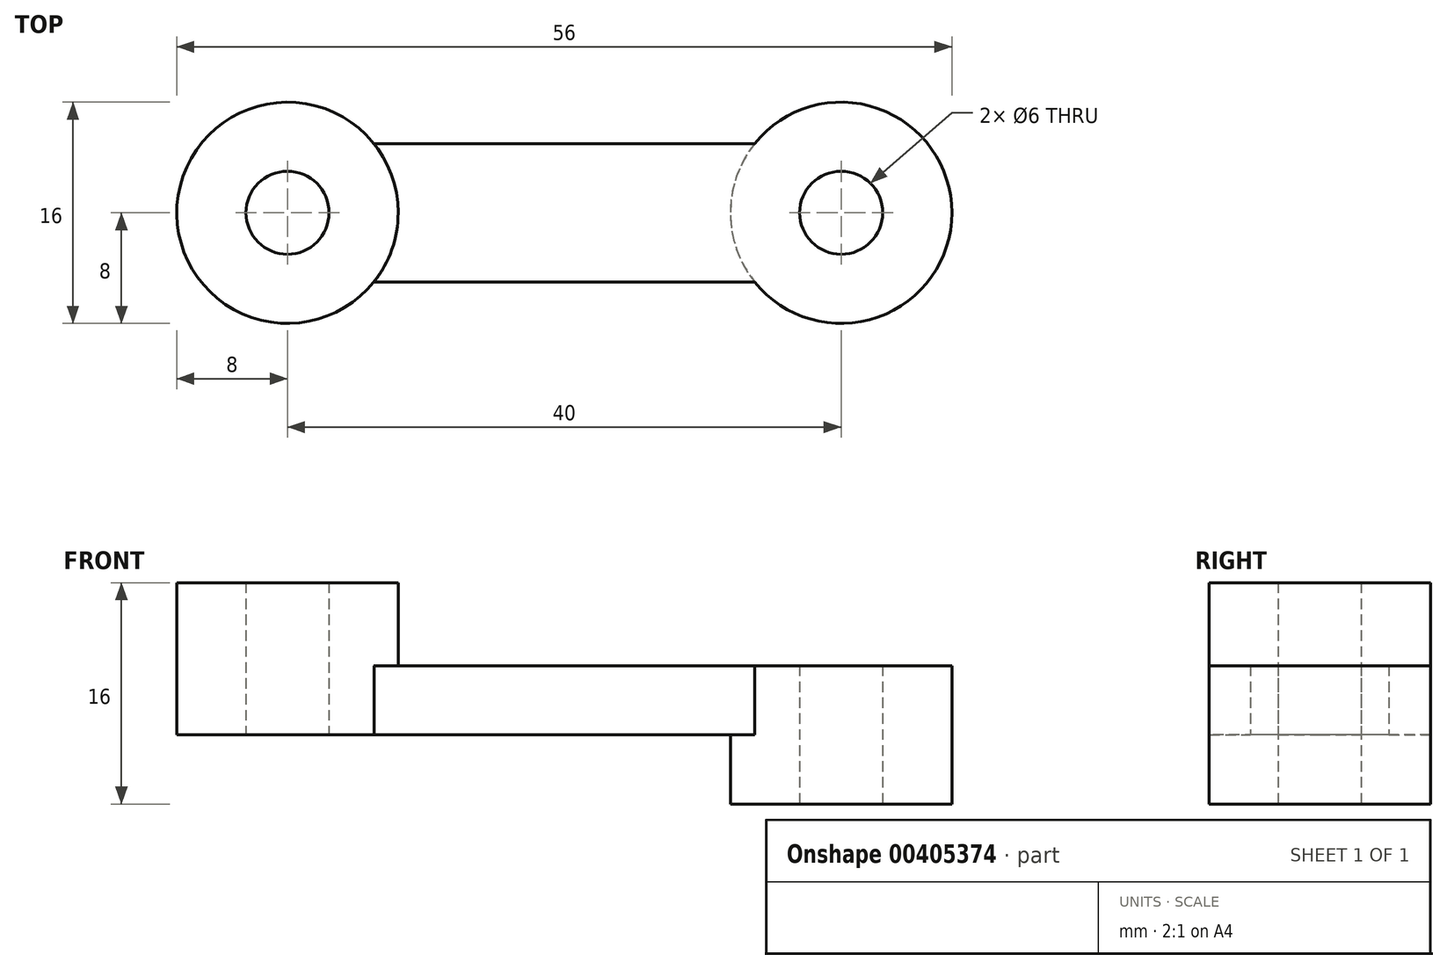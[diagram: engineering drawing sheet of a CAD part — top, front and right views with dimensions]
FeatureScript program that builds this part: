
annotation { "Feature Type Name" : "Feature", "Feature Type Description" : "" }
export const myFeature = defineFeature(function(context is Context, id is Id, definition is map)
    precondition{}
    {
        {
            var Q0;
            Q0=qCreatedBy(makeId("Top.planeOp"),FACE);
            var sketch = newSketch(context, id + "F0", { "sketchPlane" : qUnion([Q0])});
            skLineSegment(sketch, "E0.bottom", {"start": v(-13.76, 5) * mm, "end": v(13.76, 5) * mm});
            skLineSegment(sketch, "E0.top", {"start": v(-13.76, -5) * mm, "end": v(13.76, -5) * mm});
            skPoint(sketch, "E0.middle", {"position": v(0, 0) * mm});
            skArc(sketch, "E1", {"start": v(13.76, -5) * mm, "mid": v(28, 0) * mm, "end": v(13.76, 5) * mm});
            skArc(sketch, "E2", {"start": v(-13.76, 5) * mm, "mid": v(-28, 0) * mm, "end": v(-13.76, -5) * mm});
            skCircle(sketch, "E3", {"center": v(-20, 0) * mm, "radius": 3 * mm});
            skCircle(sketch, "E4", {"center": v(20, 0) * mm, "radius": 3 * mm});
            skPoint(sketch, "E5.orphan", {"position": v(-20, -5) * mm});
            skPoint(sketch, "E6.orphan", {"position": v(-20, 5) * mm});
            skPoint(sketch, "E7.orphan", {"position": v(20, 5) * mm});
            skPoint(sketch, "E0.right.end.orphan", {"position": v(20, -5) * mm});
            skSolve(sketch);
        }
        {
            var Q0;
            Q0=makeQuery(id+"F0.imprint","IMPRINT",FACE,{"disambiguationData":[TD([[makeQuery(id+"F0.imprint","IMPRINT",EDGE,{"derivedFrom":sQuery(id+"F0.wireOp",EDGE,"E0.bottom")}),-1.0]])]});
            extrude(context, id + "F1", {"entities" : qUnion([Q0]), "depth" : 5 * mm});
        }
        {
            var Q0;
            Q0=makeQuery(id+"F1.opExtrude","CAP_FACE",FACE,{"disambiguationData":[OSD([sQuery(id+"F0.wireOp",EDGE,"E0.bottom"),sQuery(id+"F0.wireOp",EDGE,"E0.top"),sQuery(id+"F0.wireOp",EDGE,"E1"),sQuery(id+"F0.wireOp",EDGE,"E2"),sQuery(id+"F0.wireOp",EDGE,"E3"),sQuery(id+"F0.wireOp",EDGE,"E4")])],"isStart":false});
            var sketch = newSketch(context, id + "F2", { "sketchPlane" : qUnion([Q0])});
            skCircle(sketch, "E8", {"center": v(-20, 0) * mm, "radius": 8 * mm});
            skCircle(sketch, "E9", {"center": v(-20, 0) * mm, "radius": 3 * mm});
            skSolve(sketch);
        }
        {
            var Q0;
            Q0=makeQuery(id+"F2.imprint","IMPRINT",FACE,{"disambiguationData":[TD([[makeQuery(id+"F2.imprint","IMPRINT",EDGE,{"derivedFrom":sQuery(id+"F2.wireOp",EDGE,"E8")}),1.0]])]});
            extrude(context, id + "F3", {"entities" : qUnion([Q0]), "operationType" : NewBodyOperationType.ADD, "depth" : 6 * mm});
        }
        {
            var Q0;
            Q0=makeQuery(id+"F1.opExtrude","CAP_FACE",FACE,{"disambiguationData":[OSD([sQuery(id+"F0.wireOp",EDGE,"E0.bottom"),sQuery(id+"F0.wireOp",EDGE,"E0.top"),sQuery(id+"F0.wireOp",EDGE,"E1"),sQuery(id+"F0.wireOp",EDGE,"E2"),sQuery(id+"F0.wireOp",EDGE,"E3"),sQuery(id+"F0.wireOp",EDGE,"E4")])],"isStart":true});
            var sketch = newSketch(context, id + "F4", { "sketchPlane" : qUnion([Q0])});
            skCircle(sketch, "E10", {"center": v(20, 0) * mm, "radius": 8 * mm});
            skCircle(sketch, "E11", {"center": v(20, 0) * mm, "radius": 3 * mm});
            skSolve(sketch);
        }
        {
            var Q0;
            {var subQ0=sQuery(id+"F4.wireOp",EDGE,"E10");Q0=makeQuery(id+"F4.imprint","IMPRINT",FACE,{"disambiguationData":[TD([[makeQuery(id+"F4.imprint","IMPRINT",EDGE,{"disambiguationData":[OD(0.0)],"derivedFrom":subQ0}),-1.0]])]});}
            extrude(context, id + "F5", {"entities" : qUnion([Q0]), "operationType" : NewBodyOperationType.ADD, "depth" : 5 * mm});
        }
    });
